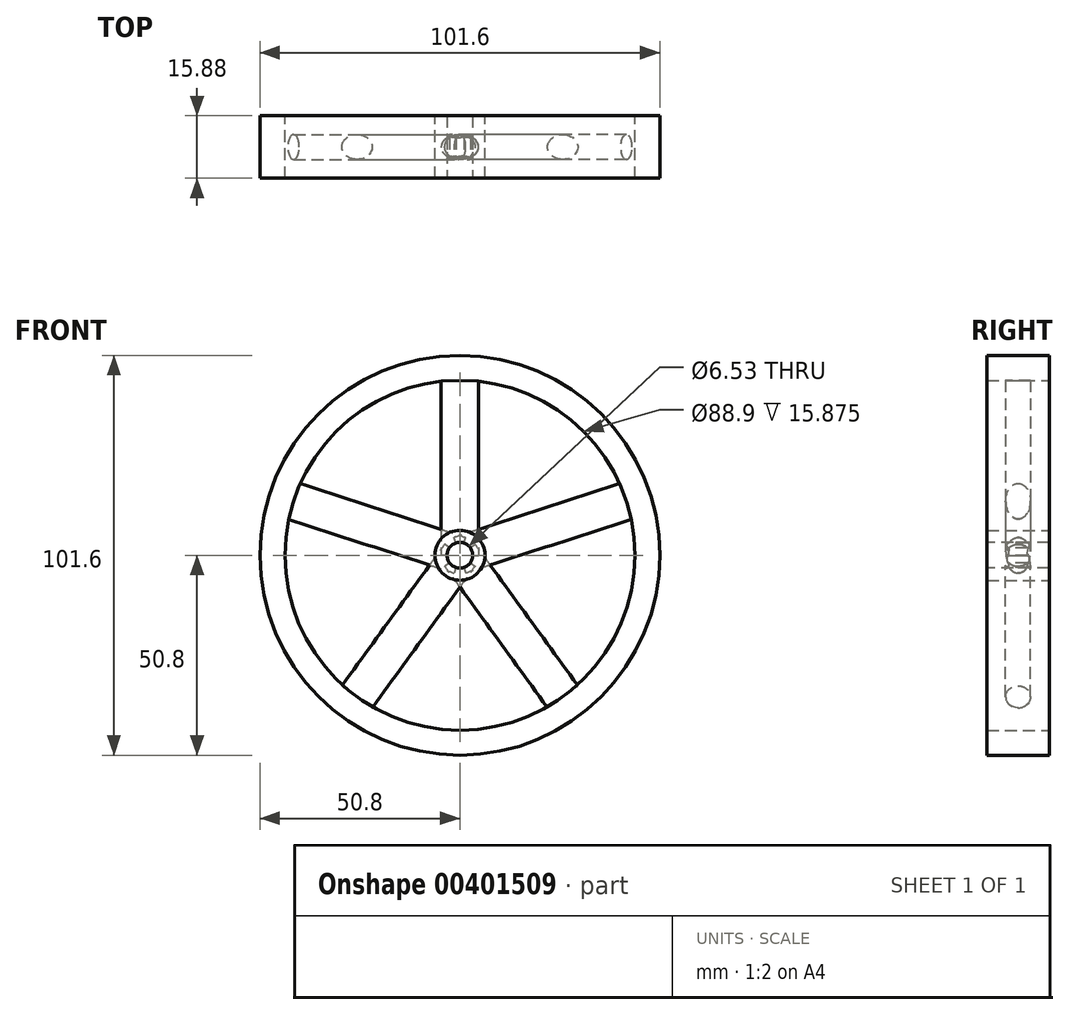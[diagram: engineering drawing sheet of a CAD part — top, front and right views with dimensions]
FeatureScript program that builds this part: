
annotation { "Feature Type Name" : "Feature", "Feature Type Description" : "" }
export const myFeature = defineFeature(function(context is Context, id is Id, definition is map)
    precondition{}
    {
        {
            var Q0;
            Q0=qCreatedBy(makeId("Front.planeOp"),FACE);
            var sketch = newSketch(context, id + "F0", { "sketchPlane" : qUnion([Q0])});
            skCircle(sketch, "E0", {"center": v(0, 0) * mm, "radius": 12.7 * mm});
            skCircle(sketch, "E1", {"center": v(0, 0) * mm, "radius": 6.35 * mm});
            skCircle(sketch, "E2", {"center": v(0, 0) * mm, "radius": 44.45 * mm});
            skCircle(sketch, "E3", {"center": v(0, 0) * mm, "radius": 50.8 * mm});
            skSolve(sketch);
        }
        {
            var Q0;
            Q0=qCreatedBy(makeId("Right.planeOp"),FACE);
            var sketch = newSketch(context, id + "F1", { "sketchPlane" : qUnion([Q0])});
            skLineSegment(sketch, "E4", {"start": v(0, 0) * mm, "end": v(-50.21, 0) * mm});
            skSolve(sketch);
        }
        {
            var Q0;
            Q0=qCreatedBy(makeId("Top.planeOp"),FACE);
            var sketch = newSketch(context, id + "F2", { "sketchPlane" : qUnion([Q0])});
            skEllipse(sketch, "E5", {"center": v(0, 0) * mm, "majorRadius": 4.76 * mm, "minorRadius": 3.18 * mm, "majorAxis": v(1, 0)});
            skSolve(sketch);
        }
        {
            var Q0;
            Q0=makeQuery(id+"F2.imprint","IMPRINT",FACE,{"disambiguationData":[TD([[makeQuery(id+"F2.imprint","IMPRINT",EDGE,{"derivedFrom":sQuery(id+"F2.wireOp",EDGE,"E5")}),1.0]])]});
            extrude(context, id + "F3", {"entities" : qUnion([Q0]), "depth" : 44.45 * mm});
        }
        {
            var Q0;
            Q0=makeQuery(id+"F3.opExtrude","SWEPT_BODY",BODY,{"disambiguationData":[OSD([sQuery(id+"F2.wireOp",EDGE,"E5")])]});
            var Q1;
            Q1=sQuery(id+"F1.wireOp",EDGE,"E4");
            circularPattern(context, id + "F4", {"entities" : qUnion([Q0]), "axis" : qUnion([Q1]), "angle" : 360 * degree, "instanceCount" : 5, "equalSpace" : true});
        }
        {
            var Q0;
            Q0=makeQuery(id+"F0.imprint","IMPRINT",FACE,{"disambiguationData":[TD([[makeQuery(id+"F0.imprint","IMPRINT",EDGE,{"derivedFrom":sQuery(id+"F0.wireOp",EDGE,"E1")}),1.0]])]});
            extrude(context, id + "F5", {"entities" : qUnion([Q0]), "endBound" : BoundingType.SYMMETRIC, "depth" : 15.88 * mm});
        }
        {
            var Q0;
            Q0=makeQuery(id+"F5.opExtrude","CAP_FACE",FACE,{"disambiguationData":[OSD([sQuery(id+"F0.wireOp",EDGE,"E1")])],"isStart":false});
            var sketch = newSketch(context, id + "F6", { "sketchPlane" : qUnion([Q0])});
            skCircle(sketch, "E6", {"center": v(0, 0) * mm, "radius": 6.35 * mm});
            skSolve(sketch);
        }
        {
            var Q0;
            Q0=sQuery(id+"F6.wireOp",VERTEX,"E6.center");
            var Q1;
            Q1=makeQuery(id+"F3.opExtrude","SWEPT_BODY",BODY,{"disambiguationData":[OSD([sQuery(id+"F2.wireOp",EDGE,"E5")])]});
            var Q2;
            Q2=makeQuery(id+"F4.opPattern","COPY",BODY,{"derivedFrom":makeQuery(id+"F3.opExtrude","SWEPT_BODY",BODY,{"disambiguationData":[OSD([sQuery(id+"F2.wireOp",EDGE,"E5")])]}),"instanceName":"1"});
            var Q3;
            Q3=makeQuery(id+"F4.opPattern","COPY",BODY,{"derivedFrom":makeQuery(id+"F3.opExtrude","SWEPT_BODY",BODY,{"disambiguationData":[OSD([sQuery(id+"F2.wireOp",EDGE,"E5")])]}),"instanceName":"2"});
            var Q4;
            Q4=makeQuery(id+"F4.opPattern","COPY",BODY,{"derivedFrom":makeQuery(id+"F3.opExtrude","SWEPT_BODY",BODY,{"disambiguationData":[OSD([sQuery(id+"F2.wireOp",EDGE,"E5")])]}),"instanceName":"3"});
            var Q5;
            Q5=makeQuery(id+"F4.opPattern","COPY",BODY,{"derivedFrom":makeQuery(id+"F3.opExtrude","SWEPT_BODY",BODY,{"disambiguationData":[OSD([sQuery(id+"F2.wireOp",EDGE,"E5")])]}),"instanceName":"4"});
            var Q6;
            Q6=makeQuery(id+"F5.opExtrude","SWEPT_BODY",BODY,{"disambiguationData":[OSD([sQuery(id+"F0.wireOp",EDGE,"E1")])]});
            hole(context, id + "F7", {"style" : HoleStyle.SIMPLE, "endStyle" : HoleEndStyle.THROUGH, "standardTappedOrClearance" : lookupTablePath({ "standard" : "ANSI", "fit" : "Close", "size" : "1/4", "type" : "Clearance" }), "standardBlindInLast" : lookupTablePath({ "fit" : "Close", "standard" : "ANSI", "size" : "1/4", "type" : "Clearance" }), "holeDiameter" : 6.53 * mm, "isTappedThrough" : true, "tappedDepth" : 12.7 * mm, "tapClearance" : 3, "locations" : qUnion([Q0]), "scope" : qUnion([Q1, Q2, Q3, Q4, Q5, Q6])});
        }
        {
            var Q0;
            Q0 = qSketchRegion(id + "F0", true);
            extrude(context, id + "F8", {"entities" : qUnion([Q0]), "endBound" : BoundingType.SYMMETRIC, "depth" : 15.88 * mm});
        }
    });
